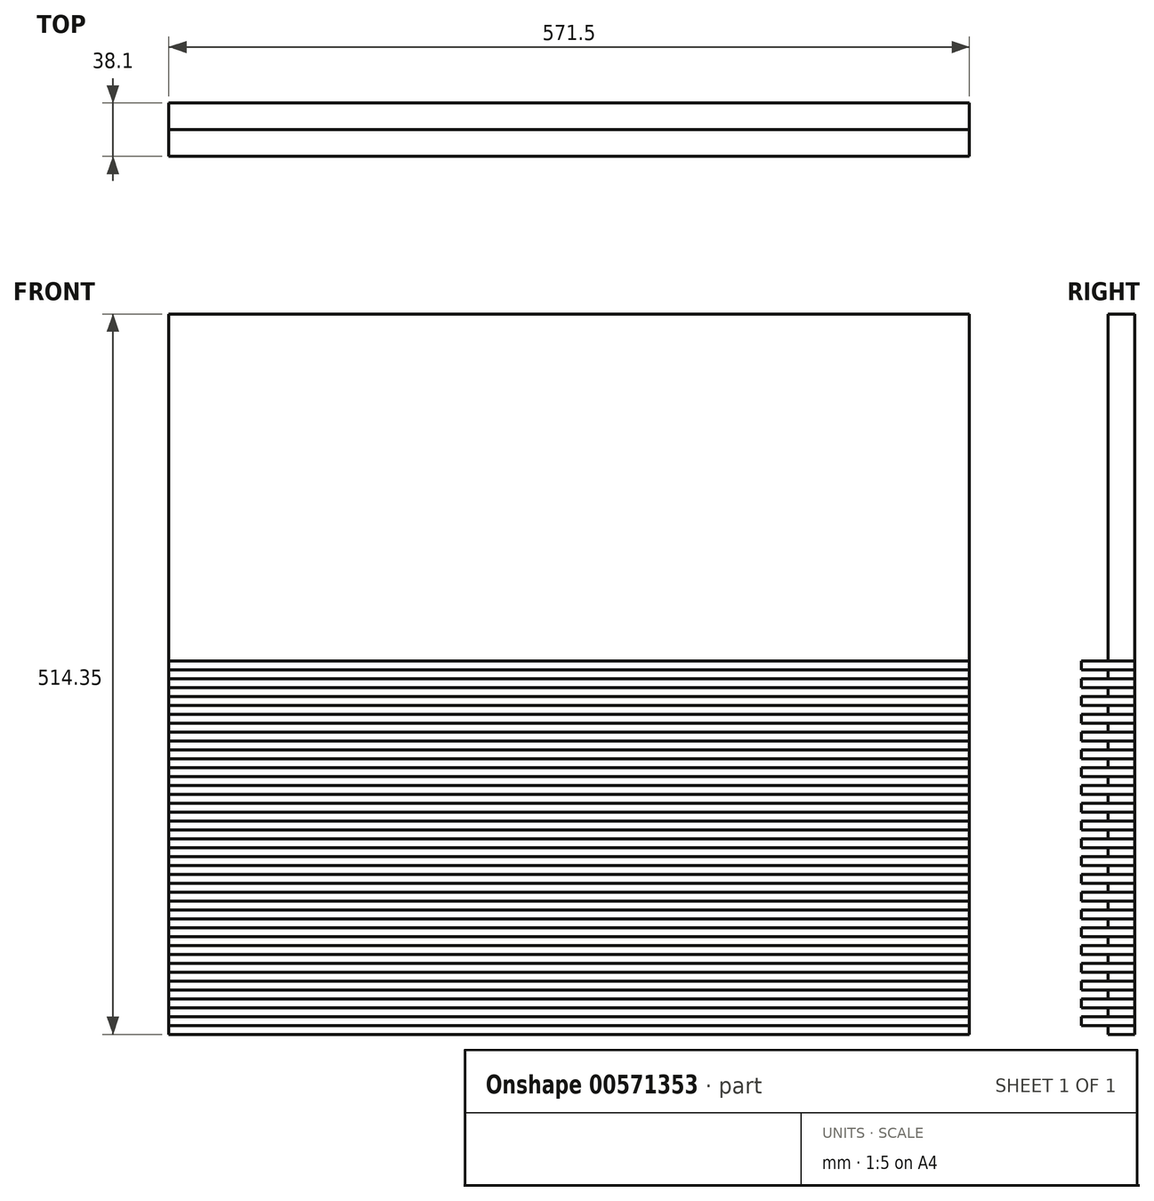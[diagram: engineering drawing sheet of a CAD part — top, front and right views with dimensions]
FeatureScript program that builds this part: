
annotation { "Feature Type Name" : "Feature", "Feature Type Description" : "" }
export const myFeature = defineFeature(function(context is Context, id is Id, definition is map)
    precondition{}
    {
        {
            var Q0;
            Q0=qCreatedBy(makeId("Front.planeOp"),FACE);
            var sketch = newSketch(context, id + "F0", { "sketchPlane" : qUnion([Q0])});
            skLineSegment(sketch, "E0.bottom", {"start": v(-313.2, 167.24) * mm, "end": v(258.3, 167.24) * mm});
            skLineSegment(sketch, "E0.top", {"start": v(-313.2, -105.81) * mm, "end": v(258.3, -105.81) * mm});
            skLineSegment(sketch, "E0.left", {"start": v(-313.2, 167.24) * mm, "end": v(-313.2, -105.81) * mm});
            skLineSegment(sketch, "E0.right", {"start": v(258.3, 167.24) * mm, "end": v(258.3, -105.81) * mm});
            skLineSegment(sketch, "E1", {"start": v(-313.2, 160.89) * mm, "end": v(258.3, 160.89) * mm});
            skLineSegment(sketch, "E2", {"start": v(-313.2, 154.54) * mm, "end": v(258.3, 154.54) * mm});
            skLineSegment(sketch, "E3", {"start": v(-313.2, 148.19) * mm, "end": v(258.3, 148.19) * mm});
            skLineSegment(sketch, "E4", {"start": v(-313.2, 141.84) * mm, "end": v(258.3, 141.84) * mm});
            skLineSegment(sketch, "E5", {"start": v(-313.2, 135.49) * mm, "end": v(258.3, 135.49) * mm});
            skLineSegment(sketch, "E6", {"start": v(-313.2, 129.14) * mm, "end": v(258.3, 129.14) * mm});
            skLineSegment(sketch, "E7", {"start": v(-313.2, 122.79) * mm, "end": v(258.3, 122.79) * mm});
            skLineSegment(sketch, "E8", {"start": v(-313.2, 116.44) * mm, "end": v(258.3, 116.44) * mm});
            skLineSegment(sketch, "E9", {"start": v(258.3, 110.09) * mm, "end": v(-313.2, 110.09) * mm});
            skLineSegment(sketch, "E10", {"start": v(258.3, 103.74) * mm, "end": v(-313.2, 103.74) * mm});
            skLineSegment(sketch, "E11", {"start": v(258.3, 91.04) * mm, "end": v(-313.2, 91.04) * mm});
            skLineSegment(sketch, "E12", {"start": v(258.3, 78.34) * mm, "end": v(-313.2, 78.34) * mm});
            skLineSegment(sketch, "E13", {"start": v(258.3, 71.99) * mm, "end": v(-313.2, 71.99) * mm});
            skLineSegment(sketch, "E14", {"start": v(258.3, 65.64) * mm, "end": v(-313.2, 65.64) * mm});
            skLineSegment(sketch, "E15", {"start": v(258.3, 84.69) * mm, "end": v(-313.2, 84.69) * mm});
            skLineSegment(sketch, "E16", {"start": v(258.3, 97.39) * mm, "end": v(-313.2, 97.39) * mm});
            skLineSegment(sketch, "E17", {"start": v(258.3, 27.54) * mm, "end": v(-313.2, 27.54) * mm});
            skLineSegment(sketch, "E18", {"start": v(258.3, 52.94) * mm, "end": v(-313.2, 52.94) * mm});
            skLineSegment(sketch, "E19", {"start": v(258.3, 46.59) * mm, "end": v(-313.2, 46.59) * mm});
            skLineSegment(sketch, "E20", {"start": v(258.3, 33.89) * mm, "end": v(-313.2, 33.89) * mm});
            skLineSegment(sketch, "E21", {"start": v(258.3, 40.24) * mm, "end": v(-313.2, 40.24) * mm});
            skLineSegment(sketch, "E22", {"start": v(258.3, 8.49) * mm, "end": v(-313.2, 8.49) * mm});
            skLineSegment(sketch, "E23", {"start": v(258.3, 14.84) * mm, "end": v(-313.2, 14.84) * mm});
            skLineSegment(sketch, "E24", {"start": v(258.3, 21.19) * mm, "end": v(-313.2, 21.19) * mm});
            skLineSegment(sketch, "E25", {"start": v(258.3, 2.14) * mm, "end": v(-313.2, 2.14) * mm});
            skLineSegment(sketch, "E26", {"start": v(258.3, 59.29) * mm, "end": v(-313.2, 59.29) * mm});
            skLineSegment(sketch, "E27", {"start": v(258.3, -23.26) * mm, "end": v(-313.2, -23.26) * mm});
            skLineSegment(sketch, "E28", {"start": v(258.3, -35.96) * mm, "end": v(-313.2, -35.96) * mm});
            skLineSegment(sketch, "E29", {"start": v(258.3, -55.01) * mm, "end": v(-313.2, -55.01) * mm});
            skLineSegment(sketch, "E30", {"start": v(258.3, -48.66) * mm, "end": v(-313.2, -48.66) * mm});
            skLineSegment(sketch, "E31", {"start": v(258.3, -16.91) * mm, "end": v(-313.2, -16.91) * mm});
            skLineSegment(sketch, "E32", {"start": v(258.3, -10.56) * mm, "end": v(-313.2, -10.56) * mm});
            skLineSegment(sketch, "E33", {"start": v(258.3, -4.21) * mm, "end": v(-313.2, -4.21) * mm});
            skLineSegment(sketch, "E34", {"start": v(258.3, -29.61) * mm, "end": v(-313.2, -29.61) * mm});
            skLineSegment(sketch, "E35", {"start": v(258.3, -61.36) * mm, "end": v(-313.2, -61.36) * mm});
            skLineSegment(sketch, "E36", {"start": v(258.3, -42.31) * mm, "end": v(-313.2, -42.31) * mm});
            skLineSegment(sketch, "E37", {"start": v(258.3, -74.06) * mm, "end": v(-313.2, -74.06) * mm});
            skLineSegment(sketch, "E38", {"start": v(258.3, -67.71) * mm, "end": v(-313.2, -67.71) * mm});
            skLineSegment(sketch, "E39", {"start": v(-313.2, -80.41) * mm, "end": v(258.3, -80.41) * mm});
            skLineSegment(sketch, "E40", {"start": v(258.3, -86.76) * mm, "end": v(-313.2, -86.76) * mm});
            skLineSegment(sketch, "E41", {"start": v(-313.2, -93.11) * mm, "end": v(258.3, -93.11) * mm});
            skLineSegment(sketch, "E42", {"start": v(258.3, -99.46) * mm, "end": v(-313.2, -99.46) * mm});
            skLineSegment(sketch, "E43", {"start": v(258.3, 167.24) * mm, "end": v(258.3, 408.54) * mm});
            skLineSegment(sketch, "E44", {"start": v(258.3, 408.54) * mm, "end": v(-313.2, 408.54) * mm});
            skLineSegment(sketch, "E45", {"start": v(-313.2, 408.54) * mm, "end": v(-313.2, 167.24) * mm});
            skSolve(sketch);
        }
        {
            var Q0;
            {var subQ0=sQuery(id+"F0.wireOp",EDGE,"V3BGaWVs-6zIW-yPpF-nYy5-btY3nBXFdGnt");Q0=makeQuery(id+"F0.imprint","IMPRINT",FACE,{"disambiguationData":[TD([[makeQuery(id+"F0.imprint","IMPRINT",EDGE,{"derivedFrom":subQ0}),1.0]])]});}
            var Q1;
            {var subQ0=sQuery(id+"F0.wireOp",EDGE,"O0JiCwPu-y2CE-ob4f-a6cF-Mzn7QjIBYwIe");Q1=makeQuery(id+"F0.imprint","IMPRINT",FACE,{"disambiguationData":[TD([[makeQuery(id+"F0.imprint","IMPRINT",EDGE,{"derivedFrom":subQ0}),1.0]])]});}
            var Q2;
            {var subQ0=sQuery(id+"F0.wireOp",EDGE,"Bf0mAokP-5thE-Pt9C-GtFq-g6FQc3eEe1Fd");Q2=makeQuery(id+"F0.imprint","IMPRINT",FACE,{"disambiguationData":[TD([[makeQuery(id+"F0.imprint","IMPRINT",EDGE,{"derivedFrom":subQ0}),1.0]])]});}
            var Q3;
            {var subQ0=sQuery(id+"F0.wireOp",EDGE,"zaXiXO8X-pKuo-okTk-NOq7-hjy3QcZZIMAn");Q3=makeQuery(id+"F0.imprint","IMPRINT",FACE,{"disambiguationData":[TD([[makeQuery(id+"F0.imprint","IMPRINT",EDGE,{"derivedFrom":subQ0}),1.0]])]});}
            var Q4;
            {var subQ0=sQuery(id+"F0.wireOp",EDGE,"IJKhDmry-Vskk-1mMp-9KlK-KMLC8J0OwIXy");Q4=makeQuery(id+"F0.imprint","IMPRINT",FACE,{"disambiguationData":[TD([[makeQuery(id+"F0.imprint","IMPRINT",EDGE,{"derivedFrom":subQ0}),-1.0]])]});}
            var Q5;
            {var subQ0=sQuery(id+"F0.wireOp",EDGE,"Rdgya41x-Z6lr-c3X9-XqZM-IwkUyTRVcvKm");Q5=makeQuery(id+"F0.imprint","IMPRINT",FACE,{"disambiguationData":[TD([[makeQuery(id+"F0.imprint","IMPRINT",EDGE,{"derivedFrom":subQ0}),1.0]])]});}
            var Q6;
            {var subQ0=sQuery(id+"F0.wireOp",EDGE,"dnMjUoUx-3DT9-Ow3q-YUgF-sidL0MO1dgpi");Q6=makeQuery(id+"F0.imprint","IMPRINT",FACE,{"disambiguationData":[TD([[makeQuery(id+"F0.imprint","IMPRINT",EDGE,{"derivedFrom":subQ0}),-1.0]])]});}
            var Q7;
            {var subQ0=sQuery(id+"F0.wireOp",EDGE,"IlW9OtLv-225t-Zoe2-lxfW-XLzdScpdTwIU");Q7=makeQuery(id+"F0.imprint","IMPRINT",FACE,{"disambiguationData":[TD([[makeQuery(id+"F0.imprint","IMPRINT",EDGE,{"derivedFrom":subQ0}),-1.0]])]});}
            var Q8;
            {var subQ0=sQuery(id+"F0.wireOp",EDGE,"J2K2s6W2-q0N7-SJ0x-0hot-NNzH9d60evkO");Q8=makeQuery(id+"F0.imprint","IMPRINT",FACE,{"disambiguationData":[TD([[makeQuery(id+"F0.imprint","IMPRINT",EDGE,{"derivedFrom":subQ0}),1.0]])]});}
            var Q9;
            {var subQ0=sQuery(id+"F0.wireOp",EDGE,"CgUwo54T-k9ZA-XLIG-t26s-Pu10vlEeWPpL");Q9=makeQuery(id+"F0.imprint","IMPRINT",FACE,{"disambiguationData":[TD([[makeQuery(id+"F0.imprint","IMPRINT",EDGE,{"derivedFrom":subQ0}),-1.0]])]});}
            var Q10;
            {var subQ0=sQuery(id+"F0.wireOp",EDGE,"ziTcAbWp-pPeh-DxRV-rrlg-XNV7XcI4THRF");Q10=makeQuery(id+"F0.imprint","IMPRINT",FACE,{"disambiguationData":[TD([[makeQuery(id+"F0.imprint","IMPRINT",EDGE,{"derivedFrom":subQ0}),-1.0]])]});}
            var Q11;
            {var subQ0=sQuery(id+"F0.wireOp",EDGE,"NEYmz5ue-G8vN-XKnl-3dFv-Z22qycUDVisV");Q11=makeQuery(id+"F0.imprint","IMPRINT",FACE,{"disambiguationData":[TD([[makeQuery(id+"F0.imprint","IMPRINT",EDGE,{"derivedFrom":subQ0}),1.0]])]});}
            var Q12;
            {var subQ0=sQuery(id+"F0.wireOp",EDGE,"mjyAoF5f-Hsy0-FT9E-tze9-ckRAjIl52L7C");Q12=makeQuery(id+"F0.imprint","IMPRINT",FACE,{"disambiguationData":[TD([[makeQuery(id+"F0.imprint","IMPRINT",EDGE,{"derivedFrom":subQ0}),1.0]])]});}
            var Q13;
            {var subQ0=sQuery(id+"F0.wireOp",EDGE,"E37");Q13=makeQuery(id+"F0.imprint","IMPRINT",FACE,{"disambiguationData":[TD([[makeQuery(id+"F0.imprint","IMPRINT",EDGE,{"derivedFrom":subQ0}),-1.0]])]});}
            var Q14;
            {var subQ0=sQuery(id+"F0.wireOp",EDGE,"E30");Q14=makeQuery(id+"F0.imprint","IMPRINT",FACE,{"disambiguationData":[TD([[makeQuery(id+"F0.imprint","IMPRINT",EDGE,{"derivedFrom":subQ0}),-1.0]])]});}
            var Q15;
            {var subQ0=sQuery(id+"F0.wireOp",EDGE,"E22");Q15=makeQuery(id+"F0.imprint","IMPRINT",FACE,{"disambiguationData":[TD([[makeQuery(id+"F0.imprint","IMPRINT",EDGE,{"derivedFrom":subQ0}),1.0]])]});}
            var Q16;
            {var subQ0=sQuery(id+"F0.wireOp",EDGE,"E29");Q16=makeQuery(id+"F0.imprint","IMPRINT",FACE,{"disambiguationData":[TD([[makeQuery(id+"F0.imprint","IMPRINT",EDGE,{"derivedFrom":subQ0}),1.0]])]});}
            var Q17;
            {var subQ0=sQuery(id+"F0.wireOp",EDGE,"E28");Q17=makeQuery(id+"F0.imprint","IMPRINT",FACE,{"disambiguationData":[TD([[makeQuery(id+"F0.imprint","IMPRINT",EDGE,{"derivedFrom":subQ0}),-1.0]])]});}
            var Q18;
            {var subQ0=sQuery(id+"F0.wireOp",EDGE,"E27");Q18=makeQuery(id+"F0.imprint","IMPRINT",FACE,{"disambiguationData":[TD([[makeQuery(id+"F0.imprint","IMPRINT",EDGE,{"derivedFrom":subQ0}),-1.0]])]});}
            var Q19;
            {var subQ0=sQuery(id+"F0.wireOp",EDGE,"E32");Q19=makeQuery(id+"F0.imprint","IMPRINT",FACE,{"disambiguationData":[TD([[makeQuery(id+"F0.imprint","IMPRINT",EDGE,{"derivedFrom":subQ0}),-1.0]])]});}
            var Q20;
            {var subQ0=sQuery(id+"F0.wireOp",EDGE,"E23");Q20=makeQuery(id+"F0.imprint","IMPRINT",FACE,{"disambiguationData":[TD([[makeQuery(id+"F0.imprint","IMPRINT",EDGE,{"derivedFrom":subQ0}),-1.0]])]});}
            var Q21;
            {var subQ0=sQuery(id+"F0.wireOp",EDGE,"E17");Q21=makeQuery(id+"F0.imprint","IMPRINT",FACE,{"disambiguationData":[TD([[makeQuery(id+"F0.imprint","IMPRINT",EDGE,{"derivedFrom":subQ0}),-1.0]])]});}
            var Q22;
            {var subQ0=sQuery(id+"F0.wireOp",EDGE,"E19");Q22=makeQuery(id+"F0.imprint","IMPRINT",FACE,{"disambiguationData":[TD([[makeQuery(id+"F0.imprint","IMPRINT",EDGE,{"derivedFrom":subQ0}),1.0]])]});}
            var Q23;
            {var subQ0=sQuery(id+"F0.wireOp",EDGE,"E18");Q23=makeQuery(id+"F0.imprint","IMPRINT",FACE,{"disambiguationData":[TD([[makeQuery(id+"F0.imprint","IMPRINT",EDGE,{"derivedFrom":subQ0}),-1.0]])]});}
            var Q24;
            {var subQ0=sQuery(id+"F0.wireOp",EDGE,"E13");Q24=makeQuery(id+"F0.imprint","IMPRINT",FACE,{"disambiguationData":[TD([[makeQuery(id+"F0.imprint","IMPRINT",EDGE,{"derivedFrom":subQ0}),1.0]])]});}
            var Q25;
            {var subQ0=sQuery(id+"F0.wireOp",EDGE,"E12");Q25=makeQuery(id+"F0.imprint","IMPRINT",FACE,{"disambiguationData":[TD([[makeQuery(id+"F0.imprint","IMPRINT",EDGE,{"derivedFrom":subQ0}),-1.0]])]});}
            var Q26;
            {var subQ0=sQuery(id+"F0.wireOp",EDGE,"E11");Q26=makeQuery(id+"F0.imprint","IMPRINT",FACE,{"disambiguationData":[TD([[makeQuery(id+"F0.imprint","IMPRINT",EDGE,{"derivedFrom":subQ0}),-1.0]])]});}
            var Q27;
            {var subQ0=sQuery(id+"F0.wireOp",EDGE,"E9");Q27=makeQuery(id+"F0.imprint","IMPRINT",FACE,{"disambiguationData":[TD([[makeQuery(id+"F0.imprint","IMPRINT",EDGE,{"derivedFrom":subQ0}),1.0]])]});}
            var Q28;
            {var subQ0=sQuery(id+"F0.wireOp",EDGE,"E7");Q28=makeQuery(id+"F0.imprint","IMPRINT",FACE,{"disambiguationData":[TD([[makeQuery(id+"F0.imprint","IMPRINT",EDGE,{"derivedFrom":subQ0}),-1.0]])]});}
            var Q29;
            {var subQ0=sQuery(id+"F0.wireOp",EDGE,"E5");Q29=makeQuery(id+"F0.imprint","IMPRINT",FACE,{"disambiguationData":[TD([[makeQuery(id+"F0.imprint","IMPRINT",EDGE,{"derivedFrom":subQ0}),-1.0]])]});}
            var Q30;
            {var subQ0=sQuery(id+"F0.wireOp",EDGE,"E3");Q30=makeQuery(id+"F0.imprint","IMPRINT",FACE,{"disambiguationData":[TD([[makeQuery(id+"F0.imprint","IMPRINT",EDGE,{"derivedFrom":subQ0}),-1.0]])]});}
            var Q31;
            {var subQ0=sQuery(id+"F0.wireOp",EDGE,"E1");Q31=makeQuery(id+"F0.imprint","IMPRINT",FACE,{"disambiguationData":[TD([[makeQuery(id+"F0.imprint","IMPRINT",EDGE,{"derivedFrom":subQ0}),-1.0]])]});}
            var Q32;
            {var subQ0=sQuery(id+"F0.wireOp",EDGE,"E39");Q32=makeQuery(id+"F0.imprint","IMPRINT",FACE,{"disambiguationData":[TD([[makeQuery(id+"F0.imprint","IMPRINT",EDGE,{"derivedFrom":subQ0}),-1.0]])]});}
            var Q33;
            {var subQ0=sQuery(id+"F0.wireOp",EDGE,"E41");Q33=makeQuery(id+"F0.imprint","IMPRINT",FACE,{"disambiguationData":[TD([[makeQuery(id+"F0.imprint","IMPRINT",EDGE,{"derivedFrom":subQ0}),-1.0]])]});}
            extrude(context, id + "F1", {"entities" : qUnion([Q0, Q1, Q2, Q3, Q4, Q5, Q6, Q7, Q8, Q9, Q10, Q11, Q12, Q13, Q14, Q15, Q16, Q17, Q18, Q19, Q20, Q21, Q22, Q23, Q24, Q25, Q26, Q27, Q28, Q29, Q30, Q31, Q32, Q33]), "depth" : 38.1 * mm, "offsetDistance" : 25.4 * mm});
        }
        {
            var Q0;
            {var subQ0=sQuery(id+"F0.wireOp",EDGE,"E0.bottom");Q0=makeQuery(id+"F0.imprint","IMPRINT",FACE,{"disambiguationData":[TD([[makeQuery(id+"F0.imprint","IMPRINT",EDGE,{"derivedFrom":subQ0}),-1.0]])]});}
            var Q1;
            {var subQ0=sQuery(id+"F0.wireOp",EDGE,"E2");Q1=makeQuery(id+"F0.imprint","IMPRINT",FACE,{"disambiguationData":[TD([[makeQuery(id+"F0.imprint","IMPRINT",EDGE,{"derivedFrom":subQ0}),-1.0]])]});}
            var Q2;
            {var subQ0=sQuery(id+"F0.wireOp",EDGE,"E4");Q2=makeQuery(id+"F0.imprint","IMPRINT",FACE,{"disambiguationData":[TD([[makeQuery(id+"F0.imprint","IMPRINT",EDGE,{"derivedFrom":subQ0}),-1.0]])]});}
            var Q3;
            {var subQ0=sQuery(id+"F0.wireOp",EDGE,"E6");Q3=makeQuery(id+"F0.imprint","IMPRINT",FACE,{"disambiguationData":[TD([[makeQuery(id+"F0.imprint","IMPRINT",EDGE,{"derivedFrom":subQ0}),-1.0]])]});}
            var Q4;
            {var subQ0=sQuery(id+"F0.wireOp",EDGE,"E8");Q4=makeQuery(id+"F0.imprint","IMPRINT",FACE,{"disambiguationData":[TD([[makeQuery(id+"F0.imprint","IMPRINT",EDGE,{"derivedFrom":subQ0}),-1.0]])]});}
            var Q5;
            {var subQ0=sQuery(id+"F0.wireOp",EDGE,"E10");Q5=makeQuery(id+"F0.imprint","IMPRINT",FACE,{"disambiguationData":[TD([[makeQuery(id+"F0.imprint","IMPRINT",EDGE,{"derivedFrom":subQ0}),1.0]])]});}
            var Q6;
            {var subQ0=sQuery(id+"F0.wireOp",EDGE,"E11");Q6=makeQuery(id+"F0.imprint","IMPRINT",FACE,{"disambiguationData":[TD([[makeQuery(id+"F0.imprint","IMPRINT",EDGE,{"derivedFrom":subQ0}),1.0]])]});}
            var Q7;
            {var subQ0=sQuery(id+"F0.wireOp",EDGE,"E12");Q7=makeQuery(id+"F0.imprint","IMPRINT",FACE,{"disambiguationData":[TD([[makeQuery(id+"F0.imprint","IMPRINT",EDGE,{"derivedFrom":subQ0}),1.0]])]});}
            var Q8;
            {var subQ0=sQuery(id+"F0.wireOp",EDGE,"E14");Q8=makeQuery(id+"F0.imprint","IMPRINT",FACE,{"disambiguationData":[TD([[makeQuery(id+"F0.imprint","IMPRINT",EDGE,{"derivedFrom":subQ0}),1.0]])]});}
            var Q9;
            {var subQ0=sQuery(id+"F0.wireOp",EDGE,"E18");Q9=makeQuery(id+"F0.imprint","IMPRINT",FACE,{"disambiguationData":[TD([[makeQuery(id+"F0.imprint","IMPRINT",EDGE,{"derivedFrom":subQ0}),1.0]])]});}
            var Q10;
            {var subQ0=sQuery(id+"F0.wireOp",EDGE,"E20");Q10=makeQuery(id+"F0.imprint","IMPRINT",FACE,{"disambiguationData":[TD([[makeQuery(id+"F0.imprint","IMPRINT",EDGE,{"derivedFrom":subQ0}),-1.0]])]});}
            var Q11;
            {var subQ0=sQuery(id+"F0.wireOp",EDGE,"E17");Q11=makeQuery(id+"F0.imprint","IMPRINT",FACE,{"disambiguationData":[TD([[makeQuery(id+"F0.imprint","IMPRINT",EDGE,{"derivedFrom":subQ0}),1.0]])]});}
            var Q12;
            {var subQ0=sQuery(id+"F0.wireOp",EDGE,"E22");Q12=makeQuery(id+"F0.imprint","IMPRINT",FACE,{"disambiguationData":[TD([[makeQuery(id+"F0.imprint","IMPRINT",EDGE,{"derivedFrom":subQ0}),-1.0]])]});}
            var Q13;
            {var subQ0=sQuery(id+"F0.wireOp",EDGE,"E25");Q13=makeQuery(id+"F0.imprint","IMPRINT",FACE,{"disambiguationData":[TD([[makeQuery(id+"F0.imprint","IMPRINT",EDGE,{"derivedFrom":subQ0}),1.0]])]});}
            var Q14;
            {var subQ0=sQuery(id+"F0.wireOp",EDGE,"E31");Q14=makeQuery(id+"F0.imprint","IMPRINT",FACE,{"disambiguationData":[TD([[makeQuery(id+"F0.imprint","IMPRINT",EDGE,{"derivedFrom":subQ0}),-1.0]])]});}
            var Q15;
            {var subQ0=sQuery(id+"F0.wireOp",EDGE,"E27");Q15=makeQuery(id+"F0.imprint","IMPRINT",FACE,{"disambiguationData":[TD([[makeQuery(id+"F0.imprint","IMPRINT",EDGE,{"derivedFrom":subQ0}),1.0]])]});}
            var Q16;
            {var subQ0=sQuery(id+"F0.wireOp",EDGE,"E28");Q16=makeQuery(id+"F0.imprint","IMPRINT",FACE,{"disambiguationData":[TD([[makeQuery(id+"F0.imprint","IMPRINT",EDGE,{"derivedFrom":subQ0}),1.0]])]});}
            var Q17;
            {var subQ0=sQuery(id+"F0.wireOp",EDGE,"E29");Q17=makeQuery(id+"F0.imprint","IMPRINT",FACE,{"disambiguationData":[TD([[makeQuery(id+"F0.imprint","IMPRINT",EDGE,{"derivedFrom":subQ0}),-1.0]])]});}
            var Q18;
            {var subQ0=sQuery(id+"F0.wireOp",EDGE,"E35");Q18=makeQuery(id+"F0.imprint","IMPRINT",FACE,{"disambiguationData":[TD([[makeQuery(id+"F0.imprint","IMPRINT",EDGE,{"derivedFrom":subQ0}),1.0]])]});}
            var Q19;
            {var subQ0=sQuery(id+"F0.wireOp",EDGE,"mjyAoF5f-Hsy0-FT9E-tze9-ckRAjIl52L7C");Q19=makeQuery(id+"F0.imprint","IMPRINT",FACE,{"disambiguationData":[TD([[makeQuery(id+"F0.imprint","IMPRINT",EDGE,{"derivedFrom":subQ0}),-1.0]])]});}
            var Q20;
            {var subQ0=sQuery(id+"F0.wireOp",EDGE,"NEYmz5ue-G8vN-XKnl-3dFv-Z22qycUDVisV");Q20=makeQuery(id+"F0.imprint","IMPRINT",FACE,{"disambiguationData":[TD([[makeQuery(id+"F0.imprint","IMPRINT",EDGE,{"derivedFrom":subQ0}),-1.0]])]});}
            var Q21;
            {var subQ0=sQuery(id+"F0.wireOp",EDGE,"49iTkevX-GDUC-3XZg-dCwe-LUhQRwvxnspp");Q21=makeQuery(id+"F0.imprint","IMPRINT",FACE,{"disambiguationData":[TD([[makeQuery(id+"F0.imprint","IMPRINT",EDGE,{"derivedFrom":subQ0}),-1.0]])]});}
            var Q22;
            {var subQ0=sQuery(id+"F0.wireOp",EDGE,"ziTcAbWp-pPeh-DxRV-rrlg-XNV7XcI4THRF");Q22=makeQuery(id+"F0.imprint","IMPRINT",FACE,{"disambiguationData":[TD([[makeQuery(id+"F0.imprint","IMPRINT",EDGE,{"derivedFrom":subQ0}),1.0]])]});}
            var Q23;
            {var subQ0=sQuery(id+"F0.wireOp",EDGE,"CgUwo54T-k9ZA-XLIG-t26s-Pu10vlEeWPpL");Q23=makeQuery(id+"F0.imprint","IMPRINT",FACE,{"disambiguationData":[TD([[makeQuery(id+"F0.imprint","IMPRINT",EDGE,{"derivedFrom":subQ0}),1.0]])]});}
            var Q24;
            {var subQ0=sQuery(id+"F0.wireOp",EDGE,"xANQQsdO-2uGS-Q6Qs-BTfA-KRMpv3E6CrYA");Q24=makeQuery(id+"F0.imprint","IMPRINT",FACE,{"disambiguationData":[TD([[makeQuery(id+"F0.imprint","IMPRINT",EDGE,{"derivedFrom":subQ0}),1.0]])]});}
            var Q25;
            {var subQ0=sQuery(id+"F0.wireOp",EDGE,"C8Orp2WI-2Dea-A8ge-ACtO-oGsDSqGZqXXW");Q25=makeQuery(id+"F0.imprint","IMPRINT",FACE,{"disambiguationData":[TD([[makeQuery(id+"F0.imprint","IMPRINT",EDGE,{"derivedFrom":subQ0}),-1.0]])]});}
            var Q26;
            {var subQ0=sQuery(id+"F0.wireOp",EDGE,"dnMjUoUx-3DT9-Ow3q-YUgF-sidL0MO1dgpi");Q26=makeQuery(id+"F0.imprint","IMPRINT",FACE,{"disambiguationData":[TD([[makeQuery(id+"F0.imprint","IMPRINT",EDGE,{"derivedFrom":subQ0}),1.0]])]});}
            var Q27;
            {var subQ0=sQuery(id+"F0.wireOp",EDGE,"pnJG9OIT-vOIb-rxOn-89CT-V1k46l9jocRr");Q27=makeQuery(id+"F0.imprint","IMPRINT",FACE,{"disambiguationData":[TD([[makeQuery(id+"F0.imprint","IMPRINT",EDGE,{"derivedFrom":subQ0}),-1.0]])]});}
            var Q28;
            {var subQ0=sQuery(id+"F0.wireOp",EDGE,"IJKhDmry-Vskk-1mMp-9KlK-KMLC8J0OwIXy");Q28=makeQuery(id+"F0.imprint","IMPRINT",FACE,{"disambiguationData":[TD([[makeQuery(id+"F0.imprint","IMPRINT",EDGE,{"derivedFrom":subQ0}),1.0]])]});}
            var Q29;
            {var subQ0=sQuery(id+"F0.wireOp",EDGE,"Bf0mAokP-5thE-Pt9C-GtFq-g6FQc3eEe1Fd");Q29=makeQuery(id+"F0.imprint","IMPRINT",FACE,{"disambiguationData":[TD([[makeQuery(id+"F0.imprint","IMPRINT",EDGE,{"derivedFrom":subQ0}),-1.0]])]});}
            var Q30;
            {var subQ0=sQuery(id+"F0.wireOp",EDGE,"O0JiCwPu-y2CE-ob4f-a6cF-Mzn7QjIBYwIe");Q30=makeQuery(id+"F0.imprint","IMPRINT",FACE,{"disambiguationData":[TD([[makeQuery(id+"F0.imprint","IMPRINT",EDGE,{"derivedFrom":subQ0}),-1.0]])]});}
            var Q31;
            {var subQ0=sQuery(id+"F0.wireOp",EDGE,"R6ozjtLw-Ciug-1LOg-GN6k-OVWbRQVnAjDU");Q31=makeQuery(id+"F0.imprint","IMPRINT",FACE,{"disambiguationData":[TD([[makeQuery(id+"F0.imprint","IMPRINT",EDGE,{"derivedFrom":subQ0}),1.0]])]});}
            var Q32;
            {var subQ0=sQuery(id+"F0.wireOp",EDGE,"oGpPOMn7-gLGG-bWTk-HCb6-S0xjFsEliCG8");Q32=makeQuery(id+"F0.imprint","IMPRINT",FACE,{"disambiguationData":[TD([[makeQuery(id+"F0.imprint","IMPRINT",EDGE,{"derivedFrom":subQ0}),1.0]])]});}
            var Q33;
            {var subQ0=sQuery(id+"F0.wireOp",EDGE,"E37");Q33=makeQuery(id+"F0.imprint","IMPRINT",FACE,{"disambiguationData":[TD([[makeQuery(id+"F0.imprint","IMPRINT",EDGE,{"derivedFrom":subQ0}),1.0]])]});}
            var Q34;
            {var subQ0=sQuery(id+"F0.wireOp",EDGE,"E40");Q34=makeQuery(id+"F0.imprint","IMPRINT",FACE,{"disambiguationData":[TD([[makeQuery(id+"F0.imprint","IMPRINT",EDGE,{"derivedFrom":subQ0}),1.0]])]});}
            var Q35;
            {var subQ0=sQuery(id+"F0.wireOp",EDGE,"E0.top");Q35=makeQuery(id+"F0.imprint","IMPRINT",FACE,{"disambiguationData":[TD([[makeQuery(id+"F0.imprint","IMPRINT",EDGE,{"derivedFrom":subQ0}),1.0]])]});}
            var Q36;
            Q36=makeQuery(id+"F0.imprint","IMPRINT",FACE,{"disambiguationData":[TD([[makeQuery(id+"F0.imprint","IMPRINT",EDGE,{"derivedFrom":sQuery(id+"F0.wireOp",EDGE,"E0.bottom")}),1.0]])]});
            extrude(context, id + "F2", {"entities" : qUnion([Q0, Q1, Q2, Q3, Q4, Q5, Q6, Q7, Q8, Q9, Q10, Q11, Q12, Q13, Q14, Q15, Q16, Q17, Q18, Q19, Q20, Q21, Q22, Q23, Q24, Q25, Q26, Q27, Q28, Q29, Q30, Q31, Q32, Q33, Q34, Q35, Q36]), "depth" : 19.05 * mm, "offsetDistance" : 25.4 * mm});
        }
    });
